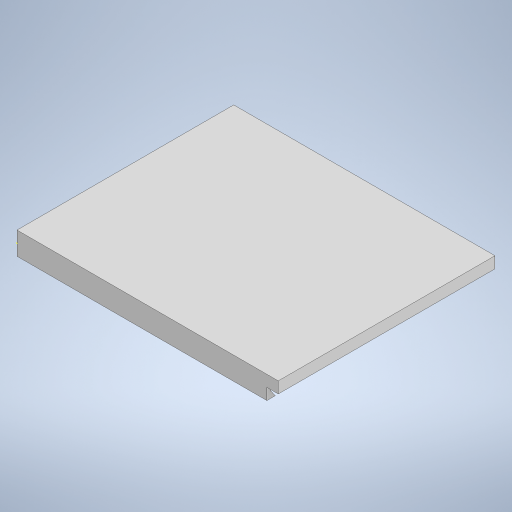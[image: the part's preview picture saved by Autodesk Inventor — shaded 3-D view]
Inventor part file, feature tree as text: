
AUTODESK INVENTOR PART (.ipt)
format: ipt  version: 2024.3 (Build 283343000, 343)  size: 207,360 bytes
history: native  units: mm
features: sketch x2, extrude x2, other x1
ambient origin geometry x8: Origin, YZ Plane, XZ Plane, XY Plane, X Axis, Y Axis, Z Axis, Center Point
bodies: Body1 (feature_tree)
feature tree (5):
  other  "Sólido1"
  sketch  "Boceto1"  dims[d0=5.0mm d1=95.4mm]
  sketch  "Boceto2"  dims[d2=5.0mm d4=3.75mm d5=1.75mm d6=2.25mm d7=0.0mm d8=110.0mm d9=0.0mm d10=115.0mm d11=0.0mm]
  extrude  "Extrusión1"  Depth=95.4mm
  extrude  "Extrusión2"  Depth=115.0mm
